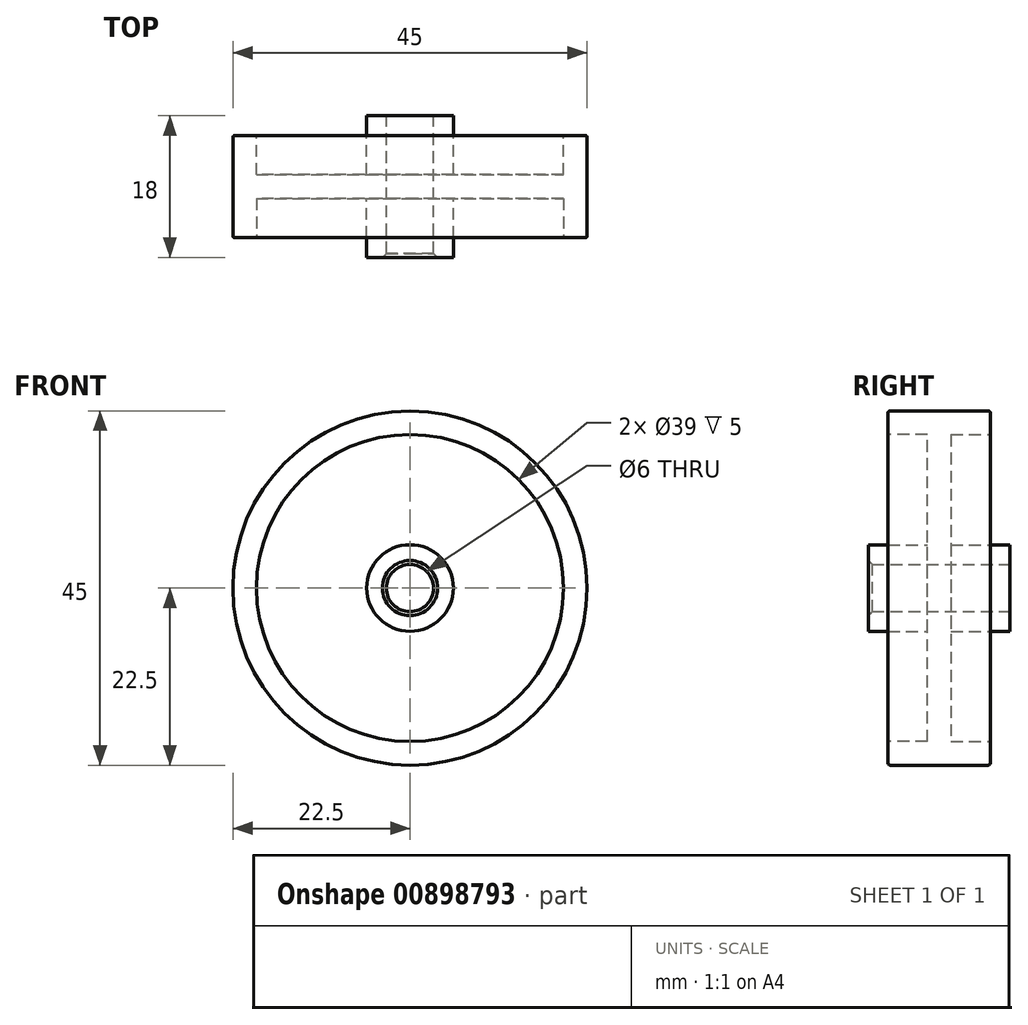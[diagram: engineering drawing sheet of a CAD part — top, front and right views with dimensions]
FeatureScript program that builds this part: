
annotation { "Feature Type Name" : "Feature", "Feature Type Description" : "" }
export const myFeature = defineFeature(function(context is Context, id is Id, definition is map)
    precondition{}
    {
        {
            var Q0;
            Q0=qCreatedBy(makeId("Front.planeOp"),FACE);
            var sketch = newSketch(context, id + "F0", { "sketchPlane" : qUnion([Q0])});
            skCircle(sketch, "E0", {"center": v(0, 0) * mm, "radius": 22.5 * mm});
            skSolve(sketch);
        }
        {
            var Q0;
            Q0 = qSketchRegion(id + "F0", true);
            extrude(context, id + "F1", {"entities" : qUnion([Q0]), "depth" : 13 * mm, "offsetDistance" : 25 * mm});
        }
        {
            var Q0;
            Q0=makeQuery(id+"F1.opExtrude","CAP_FACE",FACE,{"disambiguationData":[OSD([sQuery(id+"F0.wireOp",EDGE,"E0")])],"isStart":false});
            var sketch = newSketch(context, id + "F2", { "sketchPlane" : qUnion([Q0])});
            skCircle(sketch, "E1", {"center": v(0, 0) * mm, "radius": 19.5 * mm});
            skSolve(sketch);
        }
        {
            var Q0;
            Q0 = qSketchRegion(id + "F2", true);
            extrude(context, id + "F3", {"entities" : qUnion([Q0]), "operationType" : NewBodyOperationType.REMOVE, "oppositeDirection" : true, "depth" : 5 * mm, "offsetDistance" : 25 * mm});
        }
        {
            var Q0;
            Q0=makeQuery(id+"F1.opExtrude","CAP_FACE",FACE,{"disambiguationData":[OSD([sQuery(id+"F0.wireOp",EDGE,"E0")])],"isStart":true});
            var sketch = newSketch(context, id + "F4", { "sketchPlane" : qUnion([Q0])});
            skCircle(sketch, "E2", {"center": v(0, 0) * mm, "radius": 19.5 * mm});
            skSolve(sketch);
        }
        {
            var Q0;
            Q0 = qSketchRegion(id + "F4", true);
            extrude(context, id + "F5", {"entities" : qUnion([Q0]), "operationType" : NewBodyOperationType.REMOVE, "oppositeDirection" : true, "depth" : 5 * mm, "offsetDistance" : 25 * mm});
        }
        {
            var Q0;
            Q0=makeQuery(id+"F1.opExtrude","CAP_EDGE",EDGE,{"disambiguationData":[OSD([sQuery(id+"F0.wireOp",EDGE,"E0")])],"isStart":false});
            var Q1;
            Q1=makeQuery(id+"F1.opExtrude","CAP_EDGE",EDGE,{"disambiguationData":[OSD([sQuery(id+"F0.wireOp",EDGE,"E0")])],"isStart":true});
            var Q2;
            Q2=makeQuery(id+"F5.boolean.opBoolean","COPY",EDGE,{"derivedFrom":makeQuery(id+"F5.opExtrude","CAP_EDGE",EDGE,{"disambiguationData":[OSD([sQuery(id+"F4.wireOp",EDGE,"E2")])],"isStart":true})});
            var Q3;
            Q3=makeQuery(id+"F3.boolean.opBoolean","COPY",EDGE,{"derivedFrom":makeQuery(id+"F3.opExtrude","CAP_EDGE",EDGE,{"disambiguationData":[OSD([sQuery(id+"F2.wireOp",EDGE,"E1")])],"isStart":true})});
            fillet(context, id + "F6", {"entities" : qUnion([Q0, Q1, Q2, Q3]), "radius" : .25 * mm, "tangentPropagation" : true, "allowEdgeOverflow" : false});
        }
        {
            var Q0;
            Q0=makeQuery(id+"F3.boolean.opBoolean","COPY",FACE,{"derivedFrom":makeQuery(id+"F3.opExtrude","CAP_FACE",FACE,{"disambiguationData":[OSD([sQuery(id+"F2.wireOp",EDGE,"E1")])],"isStart":false})});
            var sketch = newSketch(context, id + "F7", { "sketchPlane" : qUnion([Q0])});
            skCircle(sketch, "E3", {"center": v(0, 0) * mm, "radius": 5.5 * mm});
            skCircle(sketch, "E4", {"center": v(0, 0) * mm, "radius": 3 * mm});
            skSolve(sketch);
        }
        {
            var Q0;
            Q0 = qSketchRegion(id + "F7", true);
            extrude(context, id + "F8", {"entities" : qUnion([Q0]), "operationType" : NewBodyOperationType.ADD, "depth" : 7.5 * mm, "offsetDistance" : 25 * mm, "hasSecondDirection" : true, "secondDirectionOppositeDirection" : true, "secondDirectionDepth" : 10.5 * mm});
        }
        {
            var Q0;
            Q0=makeQuery(id+"F8.opExtrude","CAP_FACE",FACE,{"disambiguationData":[OSD([sQuery(id+"F7.wireOp",EDGE,"E3"),sQuery(id+"F7.wireOp",EDGE,"E4")])],"isStart":false});
            var sketch = newSketch(context, id + "F9", { "sketchPlane" : qUnion([Q0])});
            skCircle(sketch, "E5", {"center": v(0, 0) * mm, "radius": 3 * mm});
            skSolve(sketch);
        }
        {
            var Q0;
            Q0 = qSketchRegion(id + "F9", true);
            extrude(context, id + "F10", {"entities" : qUnion([Q0]), "operationType" : NewBodyOperationType.REMOVE, "oppositeDirection" : true, "depth" : 25 * mm, "offsetDistance" : 25 * mm});
        }
        {
            var Q0;
            Q0=makeQuery(id+"F8.opExtrude","CAP_EDGE",EDGE,{"disambiguationData":[OSD([sQuery(id+"F7.wireOp",EDGE,"E4")])],"isStart":false});
            var Q1;
            Q1=makeQuery(id+"F8.opExtrude","CAP_EDGE",EDGE,{"disambiguationData":[OSD([sQuery(id+"F7.wireOp",EDGE,"E4")])],"isStart":true});
            chamfer(context, id + "F11", {"entities" : qUnion([Q0, Q1]), "width" : .5 * mm, "tangentPropagation" : true});
        }
    });
